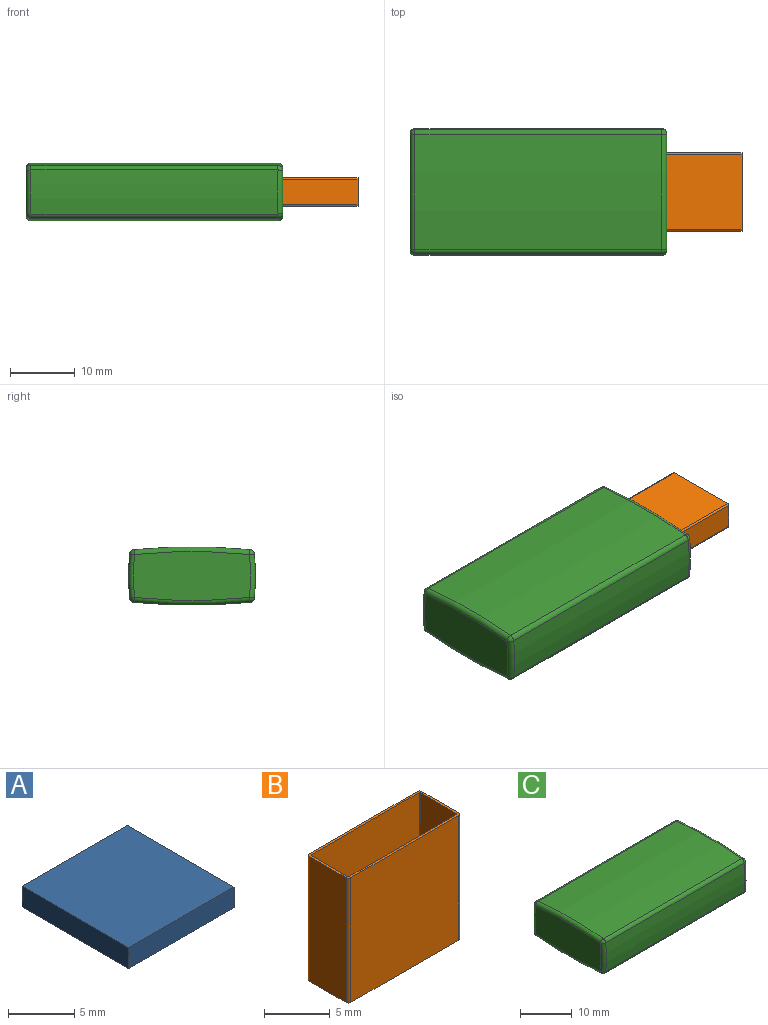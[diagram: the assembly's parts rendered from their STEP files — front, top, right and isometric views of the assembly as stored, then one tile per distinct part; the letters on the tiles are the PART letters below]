
ASSEMBLY  parts=3 mates=2
PART A: 6 faces, bbox 11.3x11.4x1.9 mm
  f0: plane 11.43x1.93mm, normal (1,0,0), area 22.1mm2, adj f1,f3,f4,f5
  f1: plane 11.43x11.25mm, normal (0,0,1), area 128.6mm2, adj f0,f2,f4,f5
  f2: plane 11.43x1.93mm, normal (-1,0,0), area 22.1mm2, adj f1,f3,f4,f5
  f3: plane 11.43x11.25mm, normal (0,0,-1), area 128.6mm2, adj f0,f2,f4,f5
  f4: plane 11.25x1.93mm, normal (0,-1,0), area 21.7mm2, adj f0,f1,f2,f3
  f5: plane 11.25x1.93mm, normal (0,1,0), area 21.7mm2, adj f0,f1,f2,f3
PART B: 18 faces, bbox 12.1x4.4x11.6 mm
  f0: plane 11.58x11.56mm, normal (0,-1,0), area 133.9mm2, adj f1,f15,f16,f17
  f1: cylinder r=0.25mm len=11.58mm, axis (0,0,-1), area 4.6mm2, adj f0,f2,f16,f17
  f2: plane 11.58x3.94mm, normal (1,0,0), area 45.6mm2, adj f1,f3,f16,f17
  f3: cylinder r=0.25mm len=11.58mm, axis (0,0,-1), area 4.6mm2, adj f2,f4,f16,f17
  f4: plane 11.58x11.56mm, normal (0,1,0), area 133.9mm2, adj f3,f5,f16,f17
  f5: cylinder r=0.25mm len=11.58mm, axis (0,0,-1), area 4.6mm2, adj f4,f6,f16,f17
  f6: plane 11.58x3.94mm, normal (-1,0,0), area 45.6mm2, adj f5,f15,f16,f17
  f7: cylinder r=0.05mm len=11.58mm, axis (0,0,-1), area 0.9mm2, adj f8,f14,f16,f17
  f8: plane 11.58x11.56mm, normal (0,1,0), area 133.9mm2, adj f7,f9,f16,f17
  f9: cylinder r=0.05mm len=11.58mm, axis (0,0,-1), area 0.9mm2, adj f8,f10,f16,f17
  f10: plane 11.58x3.94mm, normal (1,0,0), area 45.6mm2, adj f9,f11,f16,f17
  f11: cylinder r=0.05mm len=11.58mm, axis (0,0,-1), area 0.9mm2, adj f10,f12,f16,f17
  f12: plane 11.58x11.56mm, normal (0,-1,0), area 133.9mm2, adj f11,f13,f16,f17
  f13: cylinder r=0.05mm len=11.58mm, axis (0,0,-1), area 0.9mm2, adj f12,f14,f16,f17
  f14: plane 11.58x3.94mm, normal (-1,0,0), area 45.6mm2, adj f7,f13,f16,f17
  f15: cylinder r=0.25mm len=11.58mm, axis (0,0,-1), area 4.6mm2, adj f0,f6,f16,f17
  f16: plane 12.07x4.45mm, normal (0,0,1), area 6.5mm2, adj f0,f1,f2,f3,f4,f5,f6,f7
  f17: plane 12.07x4.45mm, normal (0,0,-1), area 6.5mm2, adj f0,f1,f2,f3,f4,f5,f6,f7
PART C: 26 faces, bbox 39.5x19.9x9.9 mm
  f0: cylinder r=31.63mm len=37.97mm, axis (-1,0,0), area 257.7mm2, adj f6,f9,f13,f14
  f1: cylinder r=89.55mm len=37.97mm, axis (-1,0,0), area 678.2mm2, adj f14,f19,f22,f25
  f2: cylinder r=31.63mm len=37.97mm, axis (-1,0,0), area 257.7mm2, adj f11,f20,f21,f25
  f3: cylinder r=89.55mm len=37.97mm, axis (-1,0,0), area 678.2mm2, adj f6,f10,f11,f12
  f4: plane 18.03x7.49mm, normal (1,0,0), area 128.8mm2, adj f9,f10,f19,f20
  f5: plane 18.03x7.49mm, normal (-1,0,0), area 128.8mm2, adj f12,f13,f21,f22
  f6: cylinder r=0.76mm len=37.97mm, axis (-1,0,0), area 39.5mm2, adj f0,f3,f7,f8
  f7: sphere r=0.76mm, area 0.8mm2, adj f6,f9,f10
  f8: sphere r=0.76mm, area 0.8mm2, adj f6,f12,f13
  f9: torus R=30.87mm, axis (1,0,0), area 8.1mm2, adj f0,f4,f7,f15
  f10: torus R=88.79mm, axis (1,0,0), area 21.3mm2, adj f3,f4,f7,f16
  f11: cylinder r=0.76mm len=37.97mm, axis (-1,0,0), area 39.5mm2, adj f2,f3,f16,f17
  f12: torus R=88.79mm, axis (1,0,0), area 21.3mm2, adj f3,f5,f8,f17
  f13: torus R=30.87mm, axis (1,0,0), area 8.1mm2, adj f0,f5,f8,f18
  f14: cylinder r=0.76mm len=37.97mm, axis (-1,0,0), area 39.5mm2, adj f0,f1,f15,f18
  f15: sphere r=0.76mm, area 0.8mm2, adj f9,f14,f19
  f16: sphere r=0.76mm, area 0.8mm2, adj f10,f11,f20
  f17: sphere r=0.76mm, area 0.8mm2, adj f11,f12,f21
  f18: sphere r=0.76mm, area 0.8mm2, adj f13,f14,f22
  f19: torus R=88.79mm, axis (1,0,0), area 21.3mm2, adj f1,f4,f15,f23
  f20: torus R=30.87mm, axis (1,0,0), area 8.1mm2, adj f2,f4,f16,f23
  f21: torus R=30.87mm, axis (1,0,0), area 8.1mm2, adj f2,f5,f17,f24
  f22: torus R=88.79mm, axis (1,0,0), area 21.3mm2, adj f1,f5,f18,f24
  f23: sphere r=0.76mm, area 0.8mm2, adj f19,f20,f25
  f24: sphere r=0.76mm, area 0.8mm2, adj f21,f22,f25
  f25: cylinder r=0.76mm len=37.97mm, axis (-1,0,0), area 39.5mm2, adj f1,f2,f23,f24
PLACE A rot(axis=(0,0,1),180deg) t=(45.25,-5.72,-13.2)mm
PLACE B rot(axis=(-0.58,-0.58,0.58),120deg) t=(51.08,19.14,5.8)mm
PLACE C at identity
MATE fastened B.f16 <-> C.f4  axis (-1,0,0) through (39.5,0,0)mm
MATE fastened B.f12 <-> A.f3  axis (0,0,1) through (39.5,0,-2.02)mm
